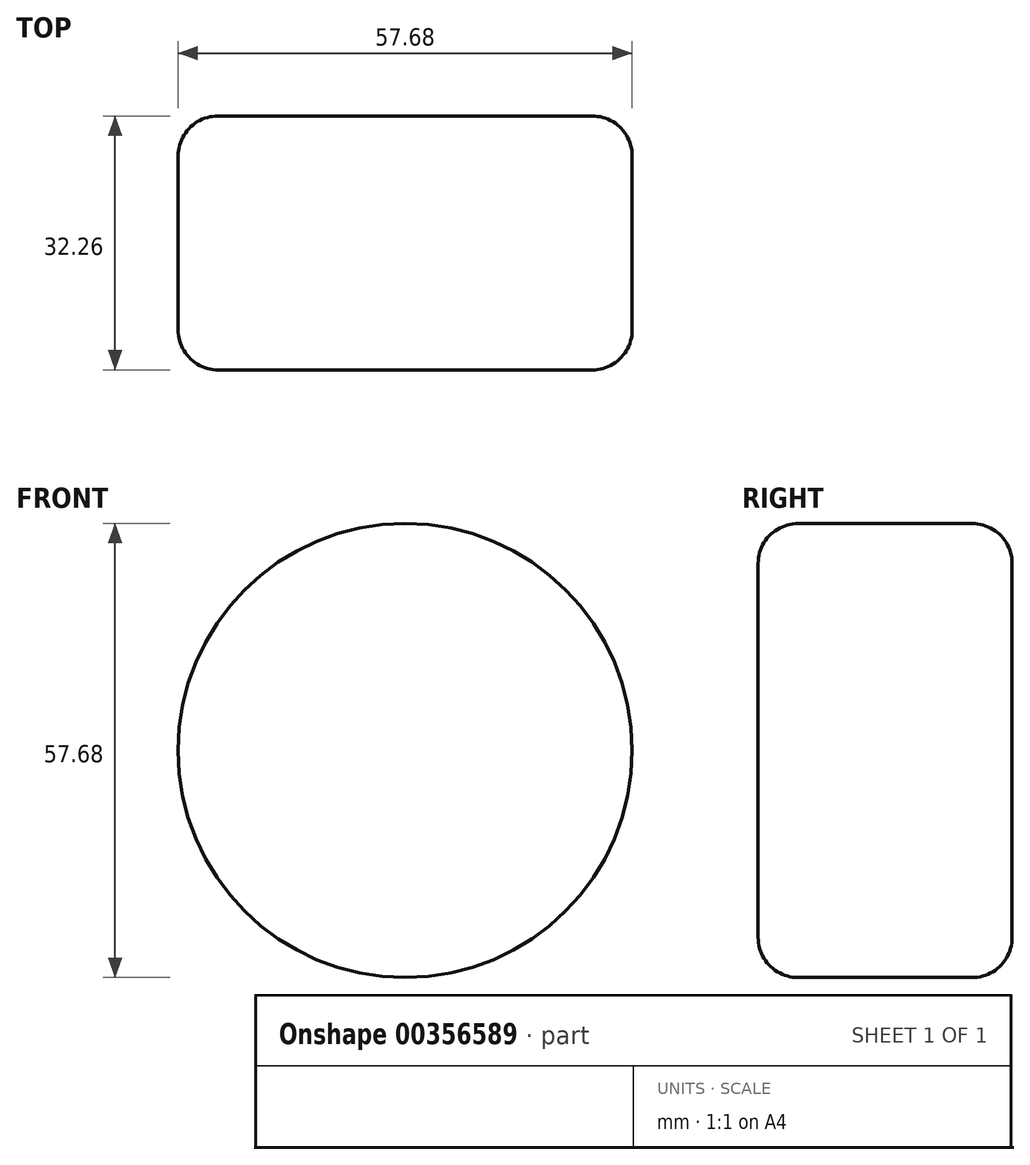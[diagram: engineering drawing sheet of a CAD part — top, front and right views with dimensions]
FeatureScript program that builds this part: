
annotation { "Feature Type Name" : "Feature", "Feature Type Description" : "" }
export const myFeature = defineFeature(function(context is Context, id is Id, definition is map)
    precondition{}
    {
        {
            var Q0;
            Q0=qCreatedBy(makeId("Front.planeOp"),FACE);
            var sketch = newSketch(context, id + "F0", { "sketchPlane" : qUnion([Q0])});
            skCircle(sketch, "E0", {"center": v(0, 0) * mm, "radius": 28.84 * mm});
            skSolve(sketch);
        }
        {
            var Q0;
            Q0=makeQuery(id+"F0.imprint","IMPRINT",FACE,{"disambiguationData":[TD([[makeQuery(id+"F0.imprint","IMPRINT",EDGE,{"derivedFrom":sQuery(id+"F0.wireOp",EDGE,"E0")}),1.0]])]});
            extrude(context, id + "F1", {"entities" : qUnion([Q0]), "depth" : 6.86 * mm});
        }
        {
            var Q0;
            Q0=makeQuery(id+"F1.opExtrude","CAP_FACE",FACE,{"disambiguationData":[OSD([sQuery(id+"F0.wireOp",EDGE,"E0")])],"isStart":false});
            extrude(context, id + "F2", {"entities" : qUnion([Q0]), "operationType" : NewBodyOperationType.ADD, "depth" : 25.4 * mm});
        }
        {
            var Q0;
            Q0=makeQuery(id+"F2.opExtrude","CAP_EDGE",EDGE,{"disambiguationData":[OSD([sQuery(id+"F0.wireOp",EDGE,"E0")])],"isStart":false});
            fillet(context, id + "F3", {"entities" : qUnion([Q0]), "radius" : 5.08 * mm, "tangentPropagation" : true, "allowEdgeOverflow" : false});
        }
        {
            var Q0;
            {var subQ0=sQuery(id+"F0.wireOp",EDGE,"E0");Q0=makeQuery(id+"F2.boolean.opBoolean","MERGE",FACE,{"derivedFrom":[makeQuery(id+"F1.opExtrude","SWEPT_FACE",FACE,{"disambiguationData":[OSD([subQ0])]}),makeQuery(id+"F2.opExtrude","SWEPT_FACE",FACE,{"disambiguationData":[OSD([subQ0])]})]});}
            fillet(context, id + "F4", {"entities" : qUnion([Q0]), "radius" : 5.08 * mm, "tangentPropagation" : true, "allowEdgeOverflow" : false});
        }
    });
